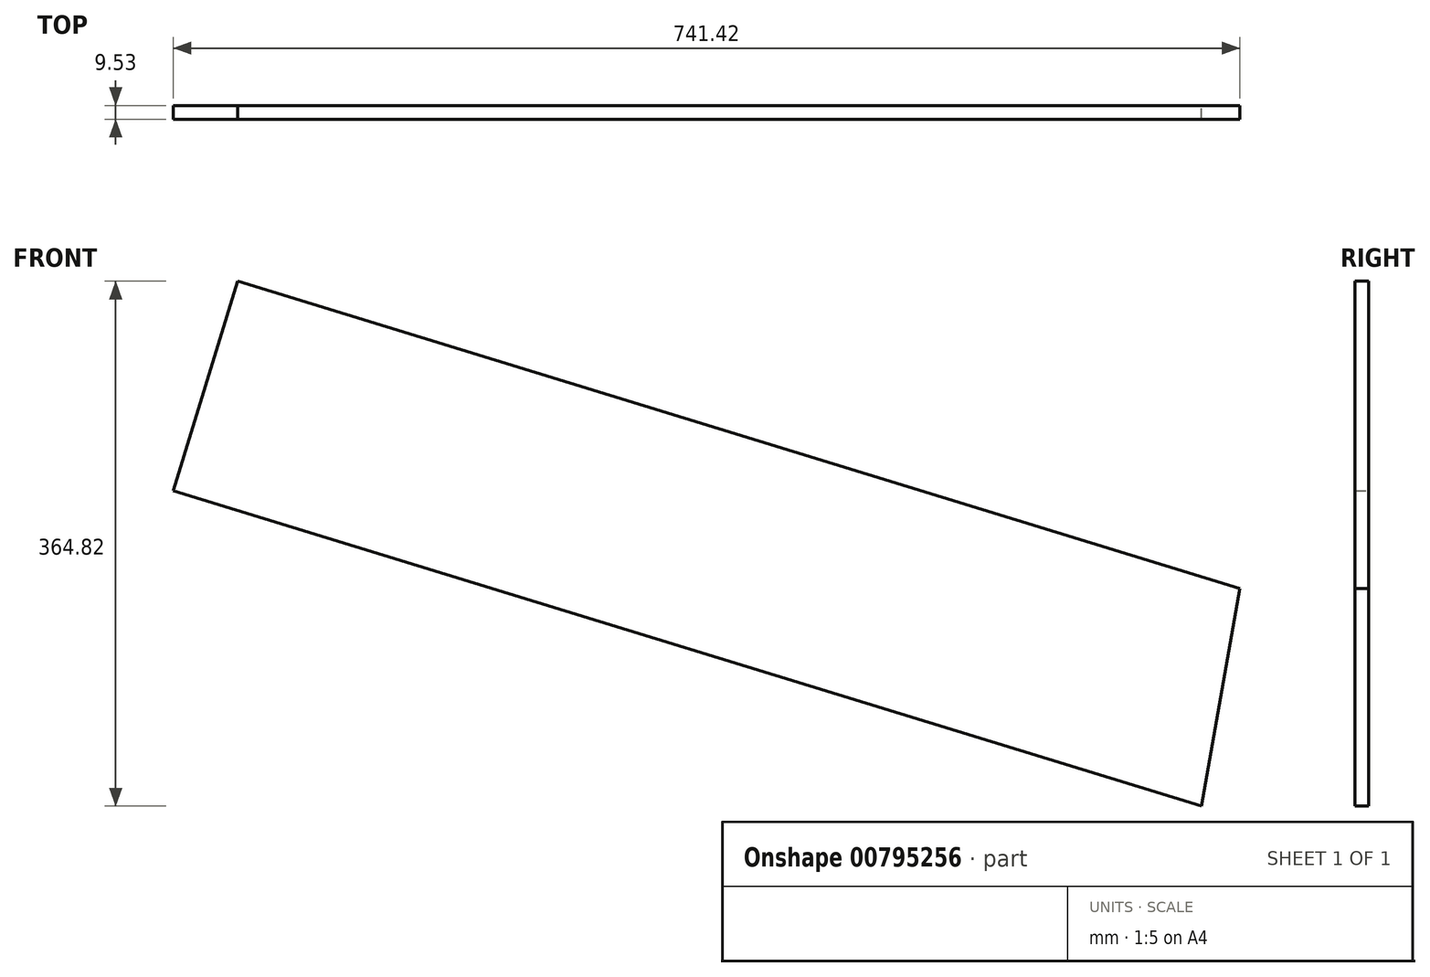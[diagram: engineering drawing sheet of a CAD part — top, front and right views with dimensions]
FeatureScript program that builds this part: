
annotation { "Feature Type Name" : "Feature", "Feature Type Description" : "" }
export const myFeature = defineFeature(function(context is Context, id is Id, definition is map)
    precondition{}
    {
        {
            var Q0;
            Q0=qCreatedBy(makeId("Front.planeOp"),FACE);
            var sketch = newSketch(context, id + "F0", { "sketchPlane" : qUnion([Q0])});
            skLineSegment(sketch, "E0", {"start": v(334.64, -15.31) * mm, "end": v(307.84, -166.5) * mm});
            skLineSegment(sketch, "E1", {"start": v(307.84, -166.5) * mm, "end": v(-406.78, 52.62) * mm});
            skLineSegment(sketch, "E2", {"start": v(-406.78, 52.62) * mm, "end": v(-362.1, 198.32) * mm});
            skLineSegment(sketch, "E3", {"start": v(-362.1, 198.32) * mm, "end": v(334.64, -15.31) * mm});
            skSolve(sketch);
        }
        {
            var Q0;
            Q0=makeQuery(id+"F0.imprint","IMPRINT",FACE,{"disambiguationData":[TD([[makeQuery(id+"F0.imprint","IMPRINT",EDGE,{"derivedFrom":sQuery(id+"F0.wireOp",EDGE,"E0")}),-1.0]])]});
            extrude(context, id + "F1", {"entities" : qUnion([Q0]), "depth" : 9.52 * mm, "offsetDistance" : 25.4 * mm});
        }
    });
